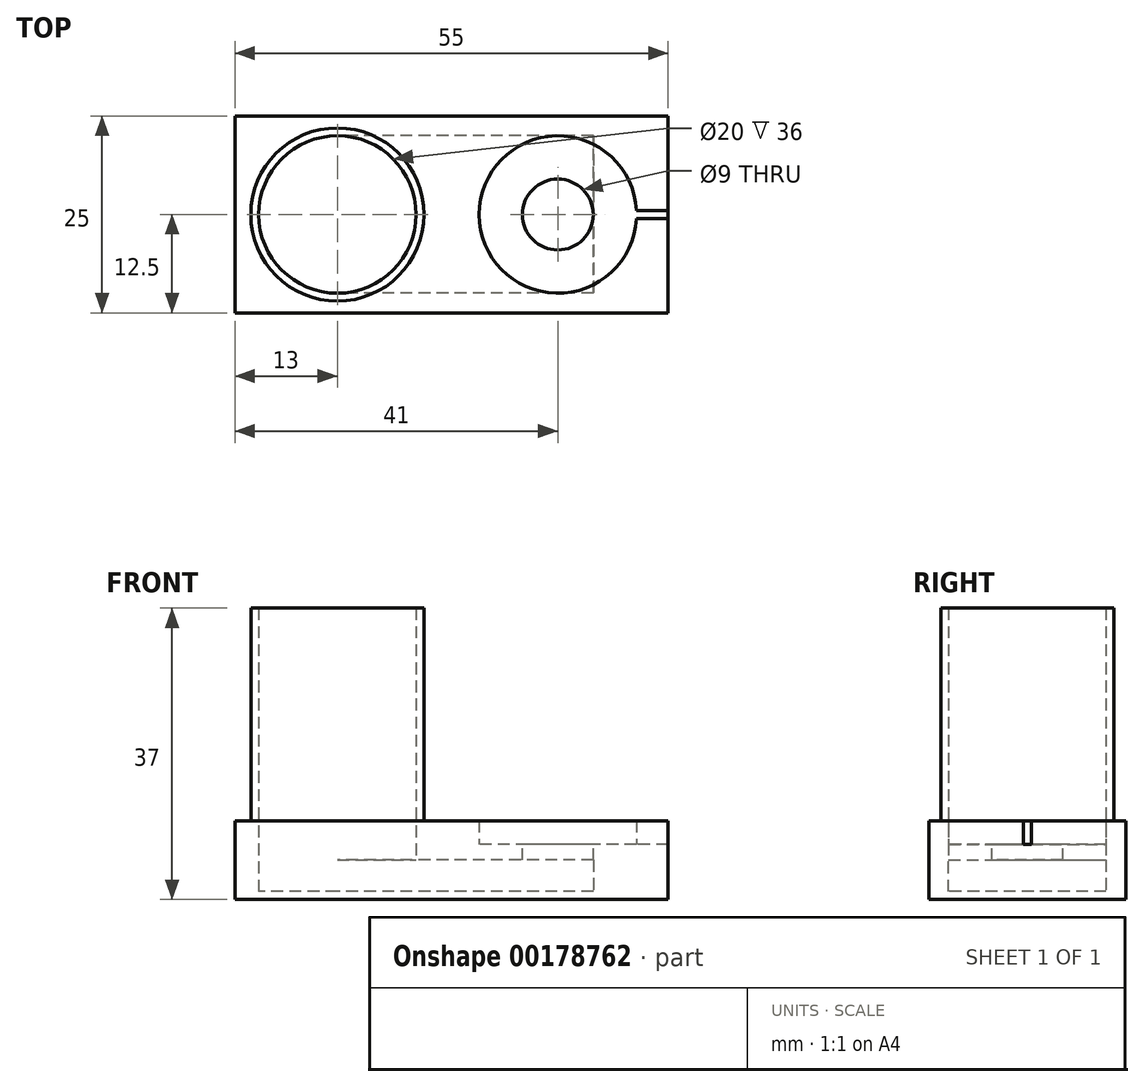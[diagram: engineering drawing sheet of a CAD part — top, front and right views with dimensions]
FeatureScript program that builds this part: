
annotation { "Feature Type Name" : "Feature", "Feature Type Description" : "" }
export const myFeature = defineFeature(function(context is Context, id is Id, definition is map)
    precondition{}
    {
        {
            var Q0;
            Q0=qCreatedBy(makeId("Top.planeOp"),FACE);
            var sketch = newSketch(context, id + "F0", { "sketchPlane" : qUnion([Q0])});
            skCircle(sketch, "E0", {"center": v(28, 0) * mm, "radius": 10 * mm});
            skCircle(sketch, "E1", {"center": v(28, 0) * mm, "radius": 4.5 * mm});
            skLineSegment(sketch, "E2.bottom", {"start": v(-13, 12.5) * mm, "end": v(42, 12.5) * mm});
            skLineSegment(sketch, "E2.top", {"start": v(-13, -12.5) * mm, "end": v(42, -12.5) * mm});
            skLineSegment(sketch, "E2.left", {"start": v(-13, 12.5) * mm, "end": v(-13, -12.5) * mm});
            skLineSegment(sketch, "E2.right", {"start": v(42, 12.5) * mm, "end": v(42, -12.5) * mm});
            skCircle(sketch, "E3", {"center": v(0, 0) * mm, "radius": 10 * mm});
            skCircle(sketch, "E4", {"center": v(0, 0) * mm, "radius": 11 * mm});
            skLineSegment(sketch, "E5", {"start": v(38, 0) * mm, "end": v(42, 0) * mm});
            skLineSegment(sketch, "E6", {"start": v(42, 0) * mm, "end": v(42, 0.5) * mm});
            skLineSegment(sketch, "E7", {"start": v(42, 0.5) * mm, "end": v(37.99, 0.5) * mm});
            skLineSegment(sketch, "E8", {"start": v(42, -0.5) * mm, "end": v(37.99, -0.5) * mm});
            skSolve(sketch);
        }
        {
            var Q0;
            Q0=makeQuery(id+"F0.imprint","IMPRINT",FACE,{"disambiguationData":[TD([[makeQuery(id+"F0.imprint","IMPRINT",EDGE,{"derivedFrom":sQuery(id+"F0.wireOp",EDGE,"E3")}),1.0]])]});
            var Q1;
            Q1=makeQuery(id+"F0.imprint","IMPRINT",FACE,{"disambiguationData":[TD([[makeQuery(id+"F0.imprint","IMPRINT",EDGE,{"derivedFrom":sQuery(id+"F0.wireOp",EDGE,"E1")}),1.0]])]});
            var Q2;
            Q2=makeQuery(id+"F0.imprint","IMPRINT",FACE,{"disambiguationData":[TD([[makeQuery(id+"F0.imprint","IMPRINT",EDGE,{"derivedFrom":sQuery(id+"F0.wireOp",EDGE,"E0")}),1.0]])]});
            var Q3;
            Q3=makeQuery(id+"F0.imprint","IMPRINT",FACE,{"disambiguationData":[TD([[makeQuery(id+"F0.imprint","IMPRINT",EDGE,{"derivedFrom":sQuery(id+"F0.wireOp",EDGE,"E0")}),-1.0]])]});
            var Q4;
            Q4=makeQuery(id+"F0.imprint","IMPRINT",FACE,{"disambiguationData":[TD([[makeQuery(id+"F0.imprint","IMPRINT",EDGE,{"derivedFrom":sQuery(id+"F0.wireOp",EDGE,"E3")}),-1.0]])]});
            var Q5;
            {var subQ0=sQuery(id+"F0.wireOp",EDGE,"E2.left");Q5=makeQuery(id+"F0.imprint","IMPRINT",FACE,{"disambiguationData":[TD([[makeQuery(id+"F0.imprint","IMPRINT",EDGE,{"derivedFrom":subQ0}),1.0]])]});}
            extrude(context, id + "F1", {"entities" : qUnion([Q0, Q1, Q2, Q3, Q4, Q5]), "depth" : 3 * mm, "hasSecondDirection" : true, "secondDirectionOppositeDirection" : true, "secondDirectionDepth" : 7 * mm});
        }
        {
            var Q0;
            Q0=makeQuery(id+"F0.imprint","IMPRINT",FACE,{"disambiguationData":[TD([[makeQuery(id+"F0.imprint","IMPRINT",EDGE,{"derivedFrom":sQuery(id+"F0.wireOp",EDGE,"E3")}),1.0]])]});
            var Q1;
            Q1=makeQuery(id+"F0.imprint","IMPRINT",FACE,{"disambiguationData":[TD([[makeQuery(id+"F0.imprint","IMPRINT",EDGE,{"derivedFrom":sQuery(id+"F0.wireOp",EDGE,"E0")}),1.0]])]});
            var Q2;
            Q2=makeQuery(id+"F0.imprint","IMPRINT",FACE,{"disambiguationData":[TD([[makeQuery(id+"F0.imprint","IMPRINT",EDGE,{"derivedFrom":sQuery(id+"F0.wireOp",EDGE,"E1")}),1.0]])]});
            var Q3;
            {var subQ0=sQuery(id+"F0.wireOp",EDGE,"E5");Q3=makeQuery(id+"F0.imprint","IMPRINT",FACE,{"disambiguationData":[TD([[makeQuery(id+"F0.imprint","IMPRINT",EDGE,{"derivedFrom":subQ0}),-1.0]])]});}
            var Q4;
            {var subQ0=sQuery(id+"F0.wireOp",EDGE,"E5");Q4=makeQuery(id+"F0.imprint","IMPRINT",FACE,{"disambiguationData":[TD([[makeQuery(id+"F0.imprint","IMPRINT",EDGE,{"derivedFrom":subQ0}),1.0]])]});}
            extrude(context, id + "F2", {"entities" : qUnion([Q0, Q1, Q2, Q3, Q4]), "operationType" : NewBodyOperationType.REMOVE, "depth" : 3 * mm});
        }
        {
            var Q0;
            Q0=makeQuery(id+"F0.imprint","IMPRINT",FACE,{"disambiguationData":[TD([[makeQuery(id+"F0.imprint","IMPRINT",EDGE,{"derivedFrom":sQuery(id+"F0.wireOp",EDGE,"E1")}),1.0]])]});
            var Q1;
            Q1=makeQuery(id+"F0.imprint","IMPRINT",FACE,{"disambiguationData":[TD([[makeQuery(id+"F0.imprint","IMPRINT",EDGE,{"derivedFrom":sQuery(id+"F0.wireOp",EDGE,"E3")}),1.0]])]});
            extrude(context, id + "F3", {"entities" : qUnion([Q0, Q1]), "operationType" : NewBodyOperationType.REMOVE, "oppositeDirection" : true, "depth" : 6 * mm});
        }
        {
            var Q0;
            Q0=qCreatedBy(makeId("Right.planeOp"),FACE);
            var sketch = newSketch(context, id + "F4", { "sketchPlane" : qUnion([Q0])});
            skLineSegment(sketch, "E9", {"start": v(10, -2) * mm, "end": v(10, -6) * mm});
            skLineSegment(sketch, "E10", {"start": v(-10, -6) * mm, "end": v(-10, -2) * mm});
            skLineSegment(sketch, "E11", {"start": v(10, 3) * mm, "end": v(10, -5) * mm});
            skLineSegment(sketch, "E12", {"start": v(10, -6) * mm, "end": v(-10, -6) * mm});
            skLineSegment(sketch, "E13", {"start": v(-10, -2) * mm, "end": v(10, -2) * mm});
            skSolve(sketch);
        }
        {
            var Q0;
            Q0=makeQuery(id+"F4.imprint","IMPRINT",FACE,{"disambiguationData":[TD([[makeQuery(id+"F4.imprint","IMPRINT",EDGE,{"derivedFrom":sQuery(id+"F4.wireOp",EDGE,"E10")}),-1.0]])]});
            extrude(context, id + "F5", {"entities" : qUnion([Q0]), "operationType" : NewBodyOperationType.REMOVE, "depth" : 32.5 * mm});
        }
        {
            var Q0;
            Q0=makeQuery(id+"F0.imprint","IMPRINT",FACE,{"disambiguationData":[TD([[makeQuery(id+"F0.imprint","IMPRINT",EDGE,{"derivedFrom":sQuery(id+"F0.wireOp",EDGE,"E3")}),-1.0]])]});
            extrude(context, id + "F6", {"entities" : qUnion([Q0]), "operationType" : NewBodyOperationType.ADD, "depth" : 30 * mm});
        }
    });
